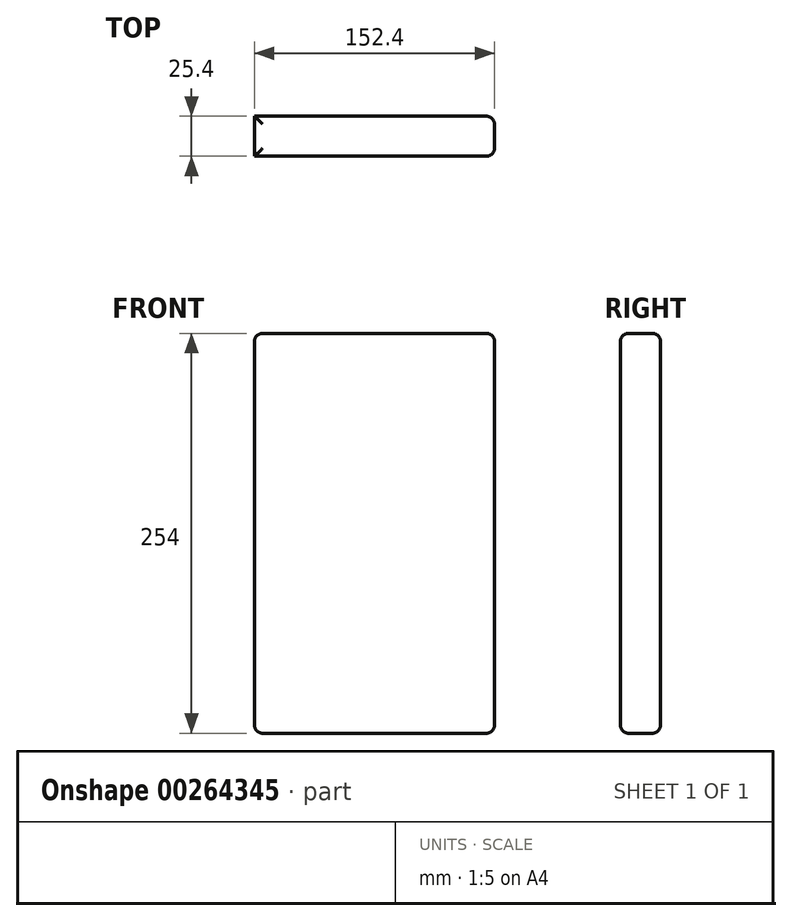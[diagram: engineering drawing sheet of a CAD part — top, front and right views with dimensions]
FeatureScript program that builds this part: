
annotation { "Feature Type Name" : "Feature", "Feature Type Description" : "" }
export const myFeature = defineFeature(function(context is Context, id is Id, definition is map)
    precondition{}
    {
        {
            var Q0;
            Q0=qCreatedBy(makeId("Front.planeOp"),FACE);
            var sketch = newSketch(context, id + "F0", { "sketchPlane" : qUnion([Q0])});
            skLineSegment(sketch, "E0.bottom", {"start": v(-76.2, -127) * mm, "end": v(76.2, -127) * mm});
            skLineSegment(sketch, "E0.top", {"start": v(-76.2, 127) * mm, "end": v(76.2, 127) * mm});
            skLineSegment(sketch, "E0.left", {"start": v(-76.2, -127) * mm, "end": v(-76.2, 127) * mm});
            skLineSegment(sketch, "E0.right", {"start": v(76.2, -127) * mm, "end": v(76.2, 127) * mm});
            skPoint(sketch, "E0.middle", {"position": v(0, 0) * mm});
            skSolve(sketch);
        }
        {
            var Q0;
            Q0=makeQuery(id+"F0.imprint","IMPRINT",FACE,{"disambiguationData":[TD([[makeQuery(id+"F0.imprint","IMPRINT",EDGE,{"derivedFrom":sQuery(id+"F0.wireOp",EDGE,"E0.bottom")}),1.0]])]});
            extrude(context, id + "F1", {"entities" : qUnion([Q0]), "depth" : 25.4 * mm});
        }
        {
            var Q0;
            Q0=makeQuery(id+"F1.opExtrude","CAP_EDGE",EDGE,{"disambiguationData":[OSD([sQuery(id+"F0.wireOp",EDGE,"E0.top")])],"isStart":false});
            var Q1;
            Q1=makeQuery(id+"F1.opExtrude","CAP_EDGE",EDGE,{"disambiguationData":[OSD([sQuery(id+"F0.wireOp",EDGE,"E0.top")])],"isStart":true});
            var Q2;
            Q2=makeQuery(id+"F1.opExtrude","SWEPT_EDGE",EDGE,{"disambiguationData":[OSD([sQuery(id+"F0.wireOp",EDGE,"E0.top"),sQuery(id+"F0.wireOp",EDGE,"E0.right")])]});
            var Q3;
            Q3=makeQuery(id+"F1.opExtrude","CAP_EDGE",EDGE,{"disambiguationData":[OSD([sQuery(id+"F0.wireOp",EDGE,"E0.right")])],"isStart":true});
            var Q4;
            Q4=makeQuery(id+"F1.opExtrude","CAP_EDGE",EDGE,{"disambiguationData":[OSD([sQuery(id+"F0.wireOp",EDGE,"E0.right")])],"isStart":false});
            var Q5;
            Q5=makeQuery(id+"F1.opExtrude","SWEPT_EDGE",EDGE,{"disambiguationData":[OSD([sQuery(id+"F0.wireOp",EDGE,"E0.bottom"),sQuery(id+"F0.wireOp",EDGE,"E0.right")])]});
            var Q6;
            Q6=makeQuery(id+"F1.opExtrude","CAP_EDGE",EDGE,{"disambiguationData":[OSD([sQuery(id+"F0.wireOp",EDGE,"E0.bottom")])],"isStart":false});
            var Q7;
            Q7=makeQuery(id+"F1.opExtrude","CAP_EDGE",EDGE,{"disambiguationData":[OSD([sQuery(id+"F0.wireOp",EDGE,"E0.bottom")])],"isStart":true});
            var Q8;
            Q8=makeQuery(id+"F1.opExtrude","SWEPT_EDGE",EDGE,{"disambiguationData":[OSD([sQuery(id+"F0.wireOp",EDGE,"E0.top"),sQuery(id+"F0.wireOp",EDGE,"E0.left")])]});
            var Q9;
            Q9=makeQuery(id+"F1.opExtrude","SWEPT_EDGE",EDGE,{"disambiguationData":[OSD([sQuery(id+"F0.wireOp",EDGE,"E0.bottom"),sQuery(id+"F0.wireOp",EDGE,"E0.left")])]});
            fillet(context, id + "F2", {"entities" : qUnion([Q0, Q1, Q2, Q3, Q4, Q5, Q6, Q7, Q8, Q9]), "radius" : 5.08 * mm, "tangentPropagation" : true, "allowEdgeOverflow" : false});
        }
    });
